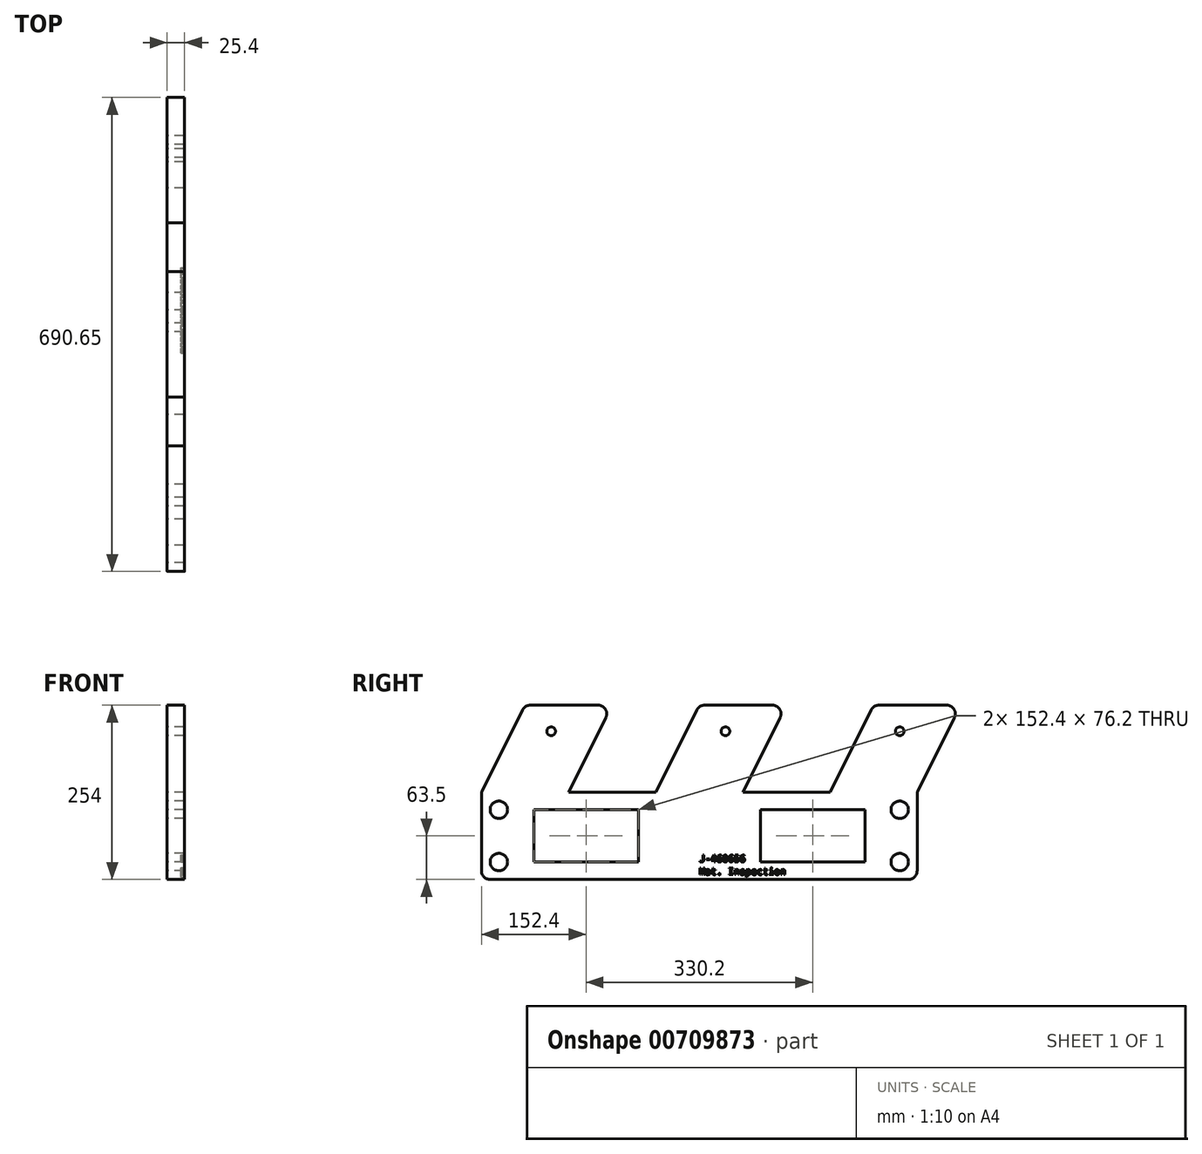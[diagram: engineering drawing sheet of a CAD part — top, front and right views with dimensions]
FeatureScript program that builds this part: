
annotation { "Feature Type Name" : "Feature", "Feature Type Description" : "" }
export const myFeature = defineFeature(function(context is Context, id is Id, definition is map)
    precondition{}
    {
        {
            var Q0;
            Q0=qCreatedBy(makeId("Right.planeOp"),FACE);
            var sketch = newSketch(context, id + "F0", { "sketchPlane" : qUnion([Q0])});
            skLineSegment(sketch, "E0.bottom", {"start": v(-317.5, 127) * mm, "end": v(317.5, 127) * mm});
            skLineSegment(sketch, "E0.top", {"start": v(-317.5, 0) * mm, "end": v(317.5, 0) * mm});
            skLineSegment(sketch, "E0.left", {"start": v(-317.5, 127) * mm, "end": v(-317.5, 0) * mm});
            skLineSegment(sketch, "E0.right", {"start": v(317.5, 127) * mm, "end": v(317.5, 0) * mm});
            skLineSegment(sketch, "E1", {"start": v(-254, 254) * mm, "end": v(381, 254) * mm});
            skLineSegment(sketch, "E2", {"start": v(-254, 254) * mm, "end": v(-317.5, 127) * mm});
            skLineSegment(sketch, "E3", {"start": v(-127, 254) * mm, "end": v(-190.5, 127) * mm});
            skLineSegment(sketch, "E4", {"start": v(0, 254) * mm, "end": v(-63.5, 127) * mm});
            skLineSegment(sketch, "E5", {"start": v(381, 254) * mm, "end": v(317.5, 127) * mm});
            skLineSegment(sketch, "E6", {"start": v(127, 254) * mm, "end": v(63.5, 127) * mm});
            skLineSegment(sketch, "E7", {"start": v(254, 254) * mm, "end": v(190.5, 127) * mm});
            skCircle(sketch, "E8", {"center": v(-215.9, 215.9) * mm, "radius": 6.35 * mm});
            skCircle(sketch, "E9", {"center": v(38.1, 215.9) * mm, "radius": 6.35 * mm});
            skCircle(sketch, "E10", {"center": v(292.1, 215.9) * mm, "radius": 6.35 * mm});
            skCircle(sketch, "E11", {"center": v(-292.1, 101.6) * mm, "radius": 12.7 * mm});
            skCircle(sketch, "E12", {"center": v(292.1, 101.6) * mm, "radius": 12.7 * mm});
            skCircle(sketch, "E13", {"center": v(-292.1, 25.4) * mm, "radius": 12.7 * mm});
            skCircle(sketch, "E14", {"center": v(292.1, 25.4) * mm, "radius": 12.7 * mm});
            skLineSegment(sketch, "E15.bottom", {"start": v(-241.3, 101.6) * mm, "end": v(-88.9, 101.6) * mm});
            skLineSegment(sketch, "E15.top", {"start": v(-241.3, 25.4) * mm, "end": v(-88.9, 25.4) * mm});
            skLineSegment(sketch, "E15.left", {"start": v(-241.3, 101.6) * mm, "end": v(-241.3, 25.4) * mm});
            skLineSegment(sketch, "E15.right", {"start": v(-88.9, 101.6) * mm, "end": v(-88.9, 25.4) * mm});
            skLineSegment(sketch, "E16.bottom", {"start": v(241.3, 101.6) * mm, "end": v(88.9, 101.6) * mm});
            skLineSegment(sketch, "E16.top", {"start": v(241.3, 25.4) * mm, "end": v(88.9, 25.4) * mm});
            skLineSegment(sketch, "E16.left", {"start": v(241.3, 101.6) * mm, "end": v(241.3, 25.4) * mm});
            skLineSegment(sketch, "E16.right", {"start": v(88.9, 101.6) * mm, "end": v(88.9, 25.4) * mm});
            skSolve(sketch);
        }
        {
            var Q0;
            Q0=makeQuery(id+"F0.imprint","IMPRINT",FACE,{"disambiguationData":[TD([[makeQuery(id+"F0.imprint","IMPRINT",EDGE,{"derivedFrom":sQuery(id+"F0.wireOp",EDGE,"E0.top")}),1.0]])]});
            var Q1;
            {var subQ1=sQuery(id+"F0.wireOp",EDGE,"E2");Q1=makeQuery(id+"F0.imprint","IMPRINT",FACE,{"disambiguationData":[TD([[makeQuery(id+"F0.imprint","IMPRINT",EDGE,{"derivedFrom":subQ1}),1.0]])]});}
            var Q2;
            {var subQ0=sQuery(id+"F0.wireOp",EDGE,"E4");Q2=makeQuery(id+"F0.imprint","IMPRINT",FACE,{"disambiguationData":[TD([[makeQuery(id+"F0.imprint","IMPRINT",EDGE,{"derivedFrom":subQ0}),1.0]])]});}
            var Q3;
            {var subQ1=sQuery(id+"F0.wireOp",EDGE,"E5");Q3=makeQuery(id+"F0.imprint","IMPRINT",FACE,{"disambiguationData":[TD([[makeQuery(id+"F0.imprint","IMPRINT",EDGE,{"derivedFrom":subQ1}),-1.0]])]});}
            extrude(context, id + "F1", {"entities" : qUnion([Q0, Q1, Q2, Q3]), "depth" : 25.4 * mm, "offsetDistance" : 25.4 * mm});
        }
        {
            var Q0;
            Q0=makeQuery(id+"F1.opExtrude","SWEPT_EDGE",EDGE,{"disambiguationData":[OSD([sQuery(id+"F0.wireOp",EDGE,"E0.top"),sQuery(id+"F0.wireOp",EDGE,"E0.left")])]});
            var Q1;
            Q1=makeQuery(id+"F1.opExtrude","SWEPT_EDGE",EDGE,{"disambiguationData":[OSD([sQuery(id+"F0.wireOp",EDGE,"E0.top"),sQuery(id+"F0.wireOp",EDGE,"E0.right")])]});
            var Q2;
            Q2=makeQuery(id+"F1.opExtrude","SWEPT_EDGE",EDGE,{"disambiguationData":[OSD([sQuery(id+"F0.wireOp",EDGE,"E1"),sQuery(id+"F0.wireOp",EDGE,"E7")])]});
            var Q3;
            Q3=makeQuery(id+"F1.opExtrude","SWEPT_EDGE",EDGE,{"disambiguationData":[OSD([sQuery(id+"F0.wireOp",EDGE,"E1"),sQuery(id+"F0.wireOp",EDGE,"E5")])]});
            var Q4;
            Q4=makeQuery(id+"F1.opExtrude","SWEPT_EDGE",EDGE,{"disambiguationData":[OSD([sQuery(id+"F0.wireOp",EDGE,"E1"),sQuery(id+"F0.wireOp",EDGE,"E6")])]});
            var Q5;
            Q5=makeQuery(id+"F1.opExtrude","SWEPT_EDGE",EDGE,{"disambiguationData":[OSD([sQuery(id+"F0.wireOp",EDGE,"E1"),sQuery(id+"F0.wireOp",EDGE,"E4")])]});
            var Q6;
            Q6=makeQuery(id+"F1.opExtrude","SWEPT_EDGE",EDGE,{"disambiguationData":[OSD([sQuery(id+"F0.wireOp",EDGE,"E1"),sQuery(id+"F0.wireOp",EDGE,"E3")])]});
            var Q7;
            Q7=makeQuery(id+"F1.opExtrude","SWEPT_EDGE",EDGE,{"disambiguationData":[OSD([sQuery(id+"F0.wireOp",EDGE,"E1"),sQuery(id+"F0.wireOp",EDGE,"E2")])]});
            var Q8;
            Q8=makeQuery(id+"F1.opExtrude","SWEPT_EDGE",EDGE,{"disambiguationData":[OSD([sQuery(id+"F0.wireOp",EDGE,"E0.bottom"),sQuery(id+"F0.wireOp",EDGE,"E0.right"),sQuery(id+"F0.wireOp",EDGE,"E5")])]});
            var Q9;
            Q9=makeQuery(id+"F1.opExtrude","SWEPT_EDGE",EDGE,{"disambiguationData":[OSD([sQuery(id+"F0.wireOp",EDGE,"E0.bottom"),sQuery(id+"F0.wireOp",EDGE,"E0.left"),sQuery(id+"F0.wireOp",EDGE,"E2")])]});
            fillet(context, id + "F2", {"entities" : qUnion([Q0, Q1, Q2, Q3, Q4, Q5, Q6, Q7, Q8, Q9]), "radius" : 12.7 * mm, "tangentPropagation" : true, "allowEdgeOverflow" : false});
        }
        {
            var Q0;
            Q0=makeQuery(id+"F1.opExtrude","CAP_FACE",FACE,{"disambiguationData":[OSD([sQuery(id+"F0.wireOp",EDGE,"E0.bottom"),sQuery(id+"F0.wireOp",EDGE,"E0.top"),sQuery(id+"F0.wireOp",EDGE,"E0.left"),sQuery(id+"F0.wireOp",EDGE,"E0.right"),sQuery(id+"F0.wireOp",EDGE,"E1"),sQuery(id+"F0.wireOp",EDGE,"E2"),sQuery(id+"F0.wireOp",EDGE,"E3"),sQuery(id+"F0.wireOp",EDGE,"E4"),sQuery(id+"F0.wireOp",EDGE,"E5"),sQuery(id+"F0.wireOp",EDGE,"E6"),sQuery(id+"F0.wireOp",EDGE,"E7"),sQuery(id+"F0.wireOp",EDGE,"E8"),sQuery(id+"F0.wireOp",EDGE,"E9"),sQuery(id+"F0.wireOp",EDGE,"E10"),sQuery(id+"F0.wireOp",EDGE,"E11"),sQuery(id+"F0.wireOp",EDGE,"E12"),sQuery(id+"F0.wireOp",EDGE,"E13"),sQuery(id+"F0.wireOp",EDGE,"E14"),sQuery(id+"F0.wireOp",EDGE,"E15.bottom"),sQuery(id+"F0.wireOp",EDGE,"E15.top"),sQuery(id+"F0.wireOp",EDGE,"E15.left"),sQuery(id+"F0.wireOp",EDGE,"E15.right"),sQuery(id+"F0.wireOp",EDGE,"E16.bottom"),sQuery(id+"F0.wireOp",EDGE,"E16.top"),sQuery(id+"F0.wireOp",EDGE,"E16.left"),sQuery(id+"F0.wireOp",EDGE,"E16.right")])],"isStart":false});
            var sketch = newSketch(context, id + "F3", { "sketchPlane" : qUnion([Q0])});
            skText(sketch, "E17", { "text": "J-460656\nMat. Inspection", "fontName": "DroidSansMono.ttf"});
            const initialGuessF3  = {"E17": [0, 0.0254, 1, 0, 0.01008]};
            skSetInitialGuess(sketch, initialGuessF3);
            skSolve(sketch);
        }
        {
            var Q0;
            Q0 = qSketchRegion(id + "F3", true);
            extrude(context, id + "F4", {"entities" : qUnion([Q0]), "operationType" : NewBodyOperationType.REMOVE, "oppositeDirection" : true, "depth" : 5.08 * mm, "offsetDistance" : 25.4 * mm});
        }
    });
